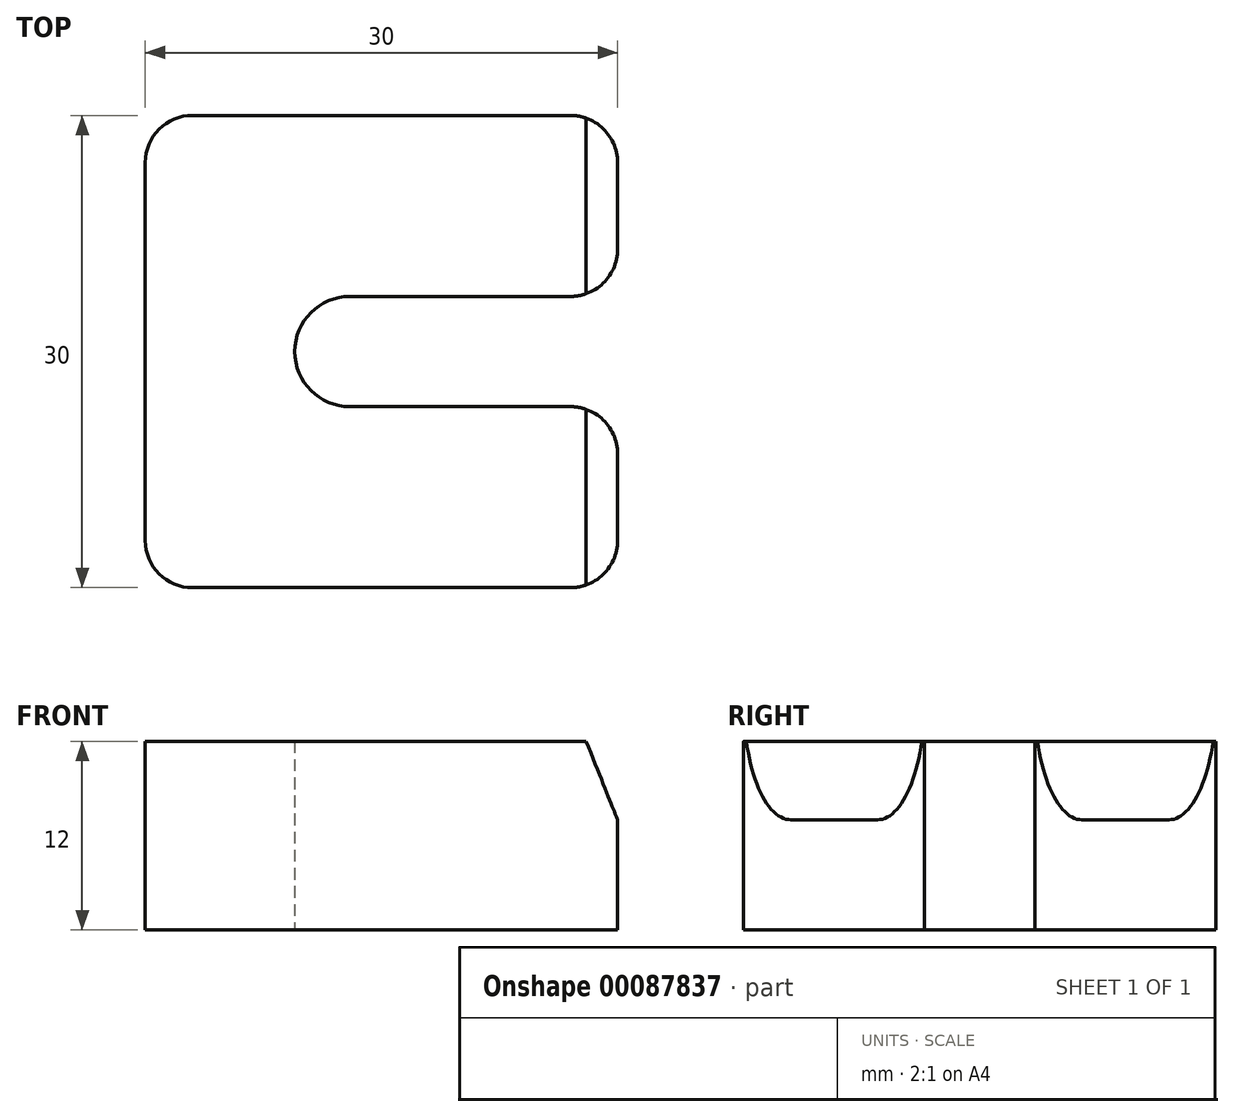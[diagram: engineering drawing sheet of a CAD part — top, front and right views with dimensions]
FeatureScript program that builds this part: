
annotation { "Feature Type Name" : "Feature", "Feature Type Description" : "" }
export const myFeature = defineFeature(function(context is Context, id is Id, definition is map)
    precondition{}
    {
        {
            assignVariable(context, id + "F0", {"name" : "thickness", "anyValue" : 12});
        }
        {
            var Q0;
            Q0=qCreatedBy(makeId("Top.planeOp"),FACE);
            var sketch = newSketch(context, id + "F1", { "sketchPlane" : qUnion([Q0])});
            skLineSegment(sketch, "E0.bottom", {"start": v(15, 15) * mm, "end": v(-15, 15) * mm});
            skLineSegment(sketch, "E0.top", {"start": v(15, -15) * mm, "end": v(-15, -15) * mm});
            skLineSegment(sketch, "E0.left", {"start": v(15, 15) * mm, "end": v(15, 3.5) * mm});
            skLineSegment(sketch, "E0.right", {"start": v(-15, 15) * mm, "end": v(-15, -15) * mm});
            skPoint(sketch, "E0.middle", {"position": v(0, 0) * mm});
            skLineSegment(sketch, "E1", {"start": v(0, 0) * mm, "end": v(42.13, 0) * mm, "construction": true});
            skArc(sketch, "E2", {"start": v(-2, 3.5) * mm, "mid": v(-5.5, 0) * mm, "end": v(-2, -3.5) * mm});
            skLineSegment(sketch, "E3", {"start": v(-2, 3.5) * mm, "end": v(15, 3.5) * mm});
            skLineSegment(sketch, "E4", {"start": v(-2, -3.5) * mm, "end": v(15, -3.5) * mm});
            skLineSegment(sketch, "E5.trimOffspring", {"start": v(15, -3.5) * mm, "end": v(15, -15) * mm});
            skSolve(sketch);
        }
        {
            var Q0;
            Q0 = qSketchRegion(id + "F1", true);
            extrude(context, id + "F2", {"entities" : qUnion([Q0]), "depth" : (getVariable(context, 'thickness')) * mm});
        }
        {
            var Q0;
            Q0=makeQuery(id+"F2.opExtrude","CAP_EDGE",EDGE,{"disambiguationData":[OSD([sQuery(id+"F1.wireOp",EDGE,"E5.trimOffspring")])],"isStart":false});
            var Q1;
            Q1=makeQuery(id+"F2.opExtrude","CAP_EDGE",EDGE,{"disambiguationData":[OSD([sQuery(id+"F1.wireOp",EDGE,"E0.left")])],"isStart":false});
            chamfer(context, id + "F3", {"entities" : qUnion([Q0, Q1]), "chamferType" : ChamferType.TWO_OFFSETS, "width1" : 2 * mm, "oppositeDirection" : false, "width2" : 5 * mm, "tangentPropagation" : true});
        }
        {
            var Q0;
            Q0=makeQuery(id+"F2.opExtrude","SWEPT_EDGE",EDGE,{"disambiguationData":[OSD([sQuery(id+"F1.wireOp",EDGE,"E0.top"),sQuery(id+"F1.wireOp",EDGE,"E0.right")])]});
            var Q1;
            Q1=makeQuery(id+"F2.opExtrude","SWEPT_EDGE",EDGE,{"disambiguationData":[OSD([sQuery(id+"F1.wireOp",EDGE,"E0.top"),sQuery(id+"F1.wireOp",EDGE,"E5.trimOffspring")])]});
            var Q2;
            Q2=makeQuery(id+"F2.opExtrude","SWEPT_EDGE",EDGE,{"disambiguationData":[OSD([sQuery(id+"F1.wireOp",EDGE,"E0.bottom"),sQuery(id+"F1.wireOp",EDGE,"E0.left")])]});
            var Q3;
            Q3=makeQuery(id+"F2.opExtrude","SWEPT_EDGE",EDGE,{"disambiguationData":[OSD([sQuery(id+"F1.wireOp",EDGE,"E0.bottom"),sQuery(id+"F1.wireOp",EDGE,"E0.right")])]});
            var Q4;
            Q4=makeQuery(id+"F2.opExtrude","SWEPT_EDGE",EDGE,{"disambiguationData":[OSD([sQuery(id+"F1.wireOp",EDGE,"E4"),sQuery(id+"F1.wireOp",EDGE,"E5.trimOffspring")])]});
            var Q5;
            Q5=makeQuery(id+"F2.opExtrude","SWEPT_EDGE",EDGE,{"disambiguationData":[OSD([sQuery(id+"F1.wireOp",EDGE,"E0.left"),sQuery(id+"F1.wireOp",EDGE,"E3")])]});
            fillet(context, id + "F4", {"entities" : qUnion([Q0, Q1, Q2, Q3, Q4, Q5]), "radius" : 3 * mm, "tangentPropagation" : true, "allowEdgeOverflow" : false});
        }
    });
